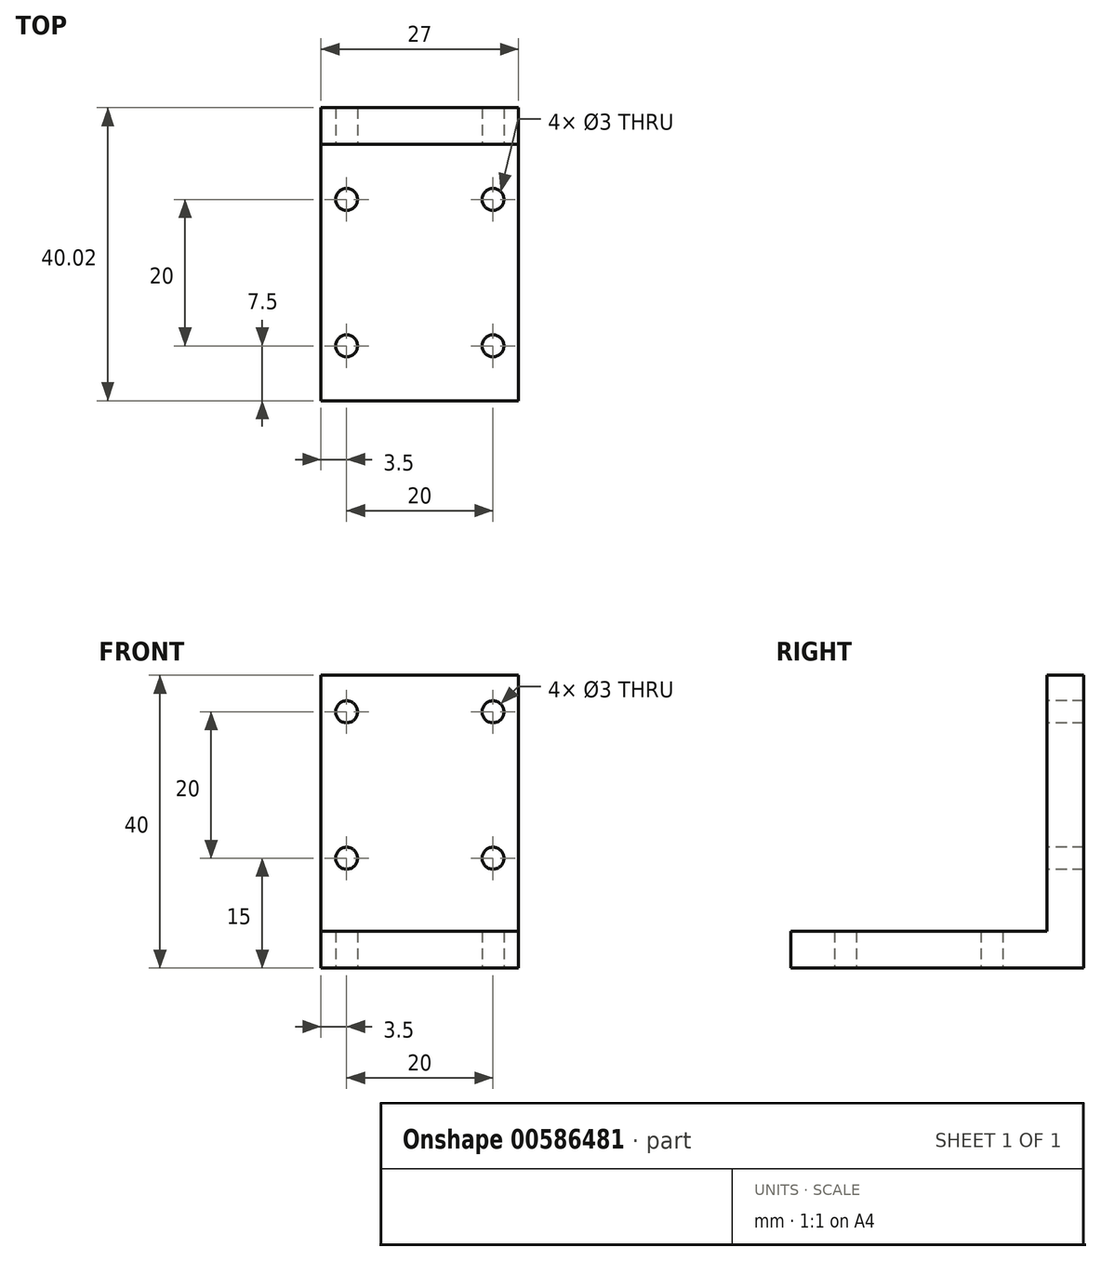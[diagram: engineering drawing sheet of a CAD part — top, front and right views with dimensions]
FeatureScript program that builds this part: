
annotation { "Feature Type Name" : "Feature", "Feature Type Description" : "" }
export const myFeature = defineFeature(function(context is Context, id is Id, definition is map)
    precondition{}
    {
        {
            var Q0;
            Q0=qCreatedBy(makeId("Top.planeOp"),FACE);
            var sketch = newSketch(context, id + "F0", { "sketchPlane" : qUnion([Q0])});
            skLineSegment(sketch, "E0.bottom", {"start": v(13.5, 17.5) * mm, "end": v(-13.5, 17.5) * mm});
            skLineSegment(sketch, "E0.top", {"start": v(13.5, -17.5) * mm, "end": v(-13.5, -17.5) * mm});
            skLineSegment(sketch, "E0.left", {"start": v(13.5, 17.5) * mm, "end": v(13.5, -17.5) * mm});
            skLineSegment(sketch, "E0.right", {"start": v(-13.5, 17.5) * mm, "end": v(-13.5, -17.5) * mm});
            skPoint(sketch, "E0.middle", {"position": v(0, 0) * mm});
            skPoint(sketch, "E1", {"position": v(-10, -10) * mm});
            skPoint(sketch, "E2.0.1.0", {"position": v(-10, 10) * mm});
            skPoint(sketch, "E2.1.0.0", {"position": v(10, -10) * mm});
            skPoint(sketch, "E2.1.1.0", {"position": v(10, 10) * mm});
            skLineSegment(sketch, "E2.direction1", {"start": v(-10, -10) * mm, "end": v(10, -10) * mm, "construction": true});
            skLineSegment(sketch, "E2.direction2", {"start": v(-10, -10) * mm, "end": v(-10, 10) * mm, "construction": true});
            skSolve(sketch);
        }
        {
            var Q0;
            Q0=makeQuery(id+"F0.imprint","IMPRINT",FACE,{"disambiguationData":[TD([[makeQuery(id+"F0.imprint","IMPRINT",EDGE,{"derivedFrom":sQuery(id+"F0.wireOp",EDGE,"E0.bottom")}),1.0]])]});
            extrude(context, id + "F1", {"entities" : qUnion([Q0]), "depth" : 5 * mm, "offsetDistance" : 25 * mm});
        }
        {
            var Q0;
            Q0=sQuery(id+"F0.wireOp",VERTEX,"E2.0.1.0");
            var Q1;
            Q1=sQuery(id+"F0.wireOp",VERTEX,"E2.1.1.0");
            var Q2;
            Q2=sQuery(id+"F0.wireOp",VERTEX,"E2.1.0.0");
            var Q3;
            Q3=sQuery(id+"F0.wireOp",VERTEX,"E1");
            var Q4;
            Q4=makeQuery(id+"F1.opExtrude","SWEPT_BODY",BODY,{"disambiguationData":[OSD([sQuery(id+"F0.wireOp",EDGE,"E0.bottom"),sQuery(id+"F0.wireOp",EDGE,"E0.top"),sQuery(id+"F0.wireOp",EDGE,"E0.left"),sQuery(id+"F0.wireOp",EDGE,"E0.right")])]});
            hole(context, id + "F2", {"style" : HoleStyle.SIMPLE, "endStyle" : HoleEndStyle.THROUGH, "oppositeDirection" : true, "holeDiameter" : 3 * mm, "majorDiameter" : 5 * mm, "isTappedThrough" : true, "tappedDepth" : 8 * mm, "tapClearance" : 3, "locations" : qUnion([Q0, Q1, Q2, Q3]), "scope" : qUnion([Q4])});
        }
        {
            var Q0;
            Q0=makeQuery(id+"F1.opExtrude","SWEPT_FACE",FACE,{"disambiguationData":[OSD([sQuery(id+"F0.wireOp",EDGE,"E0.bottom")])]});
            extrude(context, id + "F3", {"entities" : qUnion([Q0]), "operationType" : NewBodyOperationType.ADD, "depth" : 5 * mm, "offsetDistance" : 25 * mm});
        }
        {
            var Q0;
            Q0=qCreatedBy(makeId("Right.planeOp"),FACE);
            var sketch = newSketch(context, id + "F4", { "sketchPlane" : qUnion([Q0])});
            skLineSegment(sketch, "E3.bottom", {"start": v(17.52, 0) * mm, "end": v(22.52, 0) * mm});
            skLineSegment(sketch, "E3.top", {"start": v(17.52, 40) * mm, "end": v(22.52, 40) * mm});
            skLineSegment(sketch, "E3.left", {"start": v(17.52, 0) * mm, "end": v(17.52, 40) * mm});
            skLineSegment(sketch, "E3.right", {"start": v(22.52, 0) * mm, "end": v(22.52, 40) * mm});
            skSolve(sketch);
        }
        {
            var Q0;
            Q0=makeQuery(id+"F4.imprint","IMPRINT",FACE,{"disambiguationData":[TD([[makeQuery(id+"F4.imprint","IMPRINT",EDGE,{"derivedFrom":sQuery(id+"F4.wireOp",EDGE,"E3.bottom")}),1.0]])]});
            extrude(context, id + "F5", {"entities" : qUnion([Q0]), "operationType" : NewBodyOperationType.ADD, "endBound" : BoundingType.SYMMETRIC, "depth" : 27 * mm, "offsetDistance" : 25 * mm});
        }
        {
            var Q0;
            Q0=qCreatedBy(makeId("Front.planeOp"),FACE);
            var sketch = newSketch(context, id + "F6", { "sketchPlane" : qUnion([Q0])});
            skLineSegment(sketch, "E4.bottom", {"start": v(13.5, 0) * mm, "end": v(-13.5, 0) * mm});
            skLineSegment(sketch, "E4.top", {"start": v(13.5, 40) * mm, "end": v(-13.5, 40) * mm});
            skLineSegment(sketch, "E4.left", {"start": v(13.5, 0) * mm, "end": v(13.5, 40) * mm});
            skLineSegment(sketch, "E4.right", {"start": v(-13.5, 0) * mm, "end": v(-13.5, 40) * mm});
            skPoint(sketch, "E5", {"position": v(10, 35) * mm});
            skPoint(sketch, "E6.1.0.0", {"position": v(-10, 35) * mm});
            skLineSegment(sketch, "E6.direction1", {"start": v(10, 35) * mm, "end": v(-10, 35) * mm, "construction": true});
            skPoint(sketch, "E7", {"position": v(-10, 15) * mm});
            skPoint(sketch, "E8", {"position": v(10, 15) * mm});
            skSolve(sketch);
        }
        {
            var Q0;
            Q0=sQuery(id+"F6.wireOp",VERTEX,"E6.1.0.0");
            var Q1;
            Q1=sQuery(id+"F6.wireOp",VERTEX,"E5");
            var Q2;
            Q2=sQuery(id+"F6.wireOp",VERTEX,"E8");
            var Q3;
            Q3=sQuery(id+"F6.wireOp",VERTEX,"E7");
            var Q4;
            Q4=makeQuery(id+"F1.opExtrude","SWEPT_BODY",BODY,{"disambiguationData":[OSD([sQuery(id+"F0.wireOp",EDGE,"E0.bottom"),sQuery(id+"F0.wireOp",EDGE,"E0.top"),sQuery(id+"F0.wireOp",EDGE,"E0.left"),sQuery(id+"F0.wireOp",EDGE,"E0.right")])]});
            hole(context, id + "F7", {"style" : HoleStyle.SIMPLE, "endStyle" : HoleEndStyle.THROUGH, "holeDiameter" : 3 * mm, "majorDiameter" : 5 * mm, "isTappedThrough" : true, "tappedDepth" : 8 * mm, "tapClearance" : 3, "locations" : qUnion([Q0, Q1, Q2, Q3]), "scope" : qUnion([Q4])});
        }
    });
